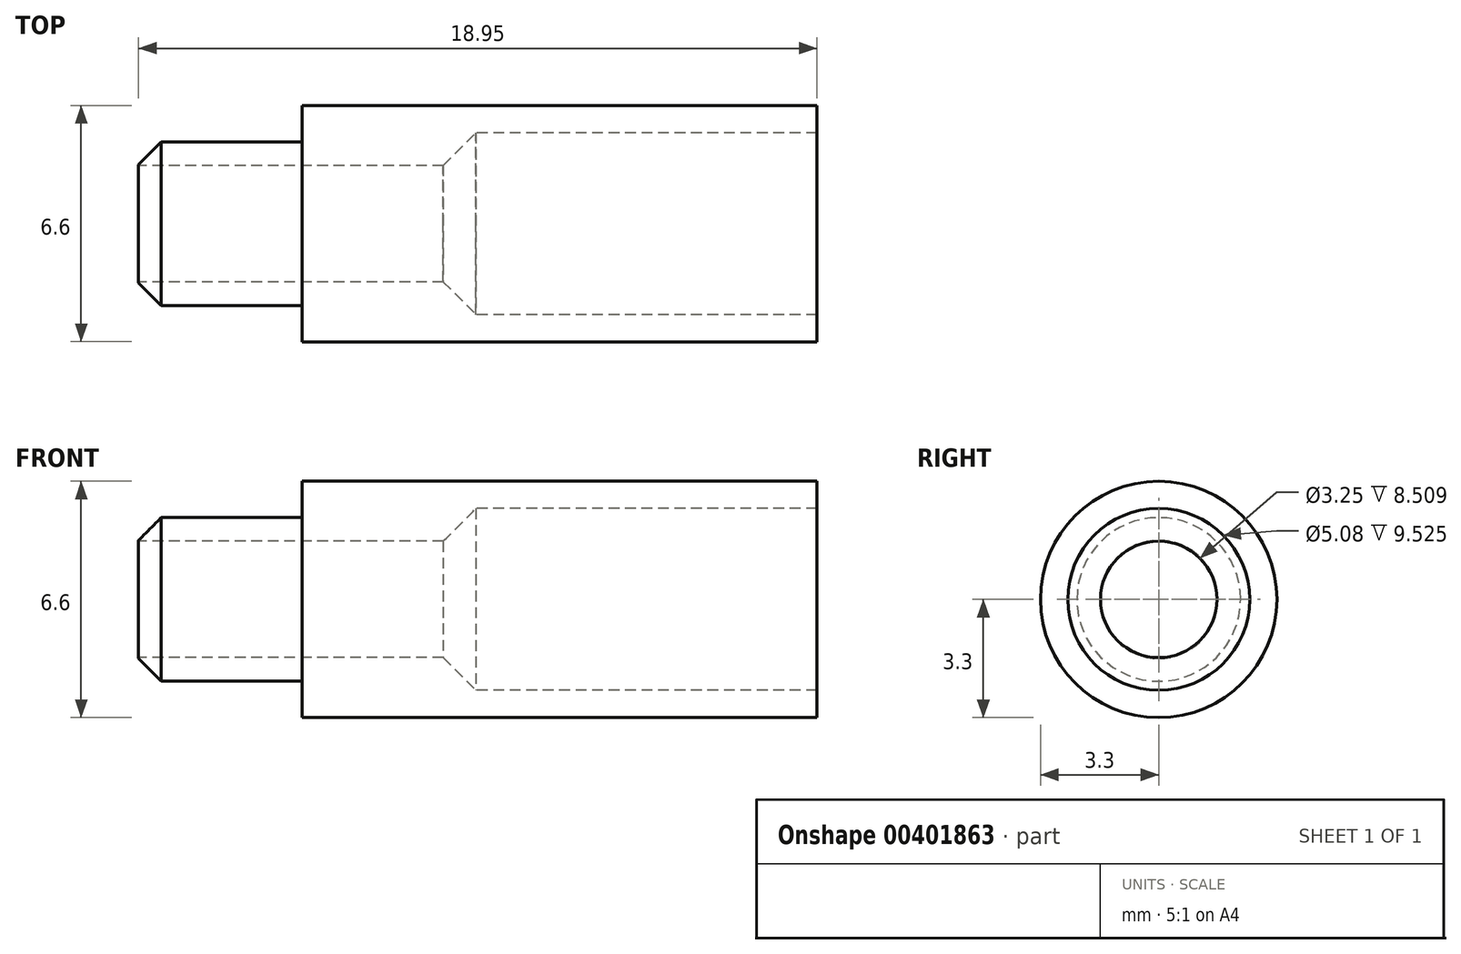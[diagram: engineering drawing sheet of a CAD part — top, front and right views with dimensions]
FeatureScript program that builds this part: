
annotation { "Feature Type Name" : "Feature", "Feature Type Description" : "" }
export const myFeature = defineFeature(function(context is Context, id is Id, definition is map)
    precondition{}
    {
        {
            var Q0;
            Q0=qCreatedBy(makeId("Front.planeOp"),FACE);
            var sketch = newSketch(context, id + "F0", { "sketchPlane" : qUnion([Q0])});
            skLineSegment(sketch, "E0", {"start": v(0, 1.63) * mm, "end": v(0, 1.65) * mm});
            skLineSegment(sketch, "E1", {"start": v(0, 1.65) * mm, "end": v(0.64, 2.29) * mm});
            skLineSegment(sketch, "E2", {"start": v(0.64, 2.29) * mm, "end": v(4.57, 2.29) * mm});
            skLineSegment(sketch, "E3", {"start": v(4.57, 2.29) * mm, "end": v(4.57, 3.3) * mm});
            skLineSegment(sketch, "E4", {"start": v(4.57, 3.3) * mm, "end": v(18.95, 3.3) * mm});
            skLineSegment(sketch, "E5", {"start": v(18.95, 3.3) * mm, "end": v(18.95, 2.54) * mm});
            skLineSegment(sketch, "E6", {"start": v(18.95, 2.54) * mm, "end": v(9.42, 2.54) * mm});
            skLineSegment(sketch, "E7", {"start": v(9.42, 2.54) * mm, "end": v(8.5, 1.63) * mm});
            skLineSegment(sketch, "E8", {"start": v(8.5, 1.63) * mm, "end": v(0, 1.63) * mm});
            skLineSegment(sketch, "E9", {"start": v(0, 0) * mm, "end": v(19.38, 0) * mm, "construction": true});
            skSolve(sketch);
        }
        {
            var Q0;
            Q0 = qSketchRegion(id + "F0", true);
            var Q1;
            Q1=sQuery(id+"F0.wireOp",EDGE,"E9");
            revolve(context, id + "F1", {"entities" : qUnion([Q0]), "axis" : qUnion([Q1]), "revolveType" : RevolveType.FULL});
        }
    });
